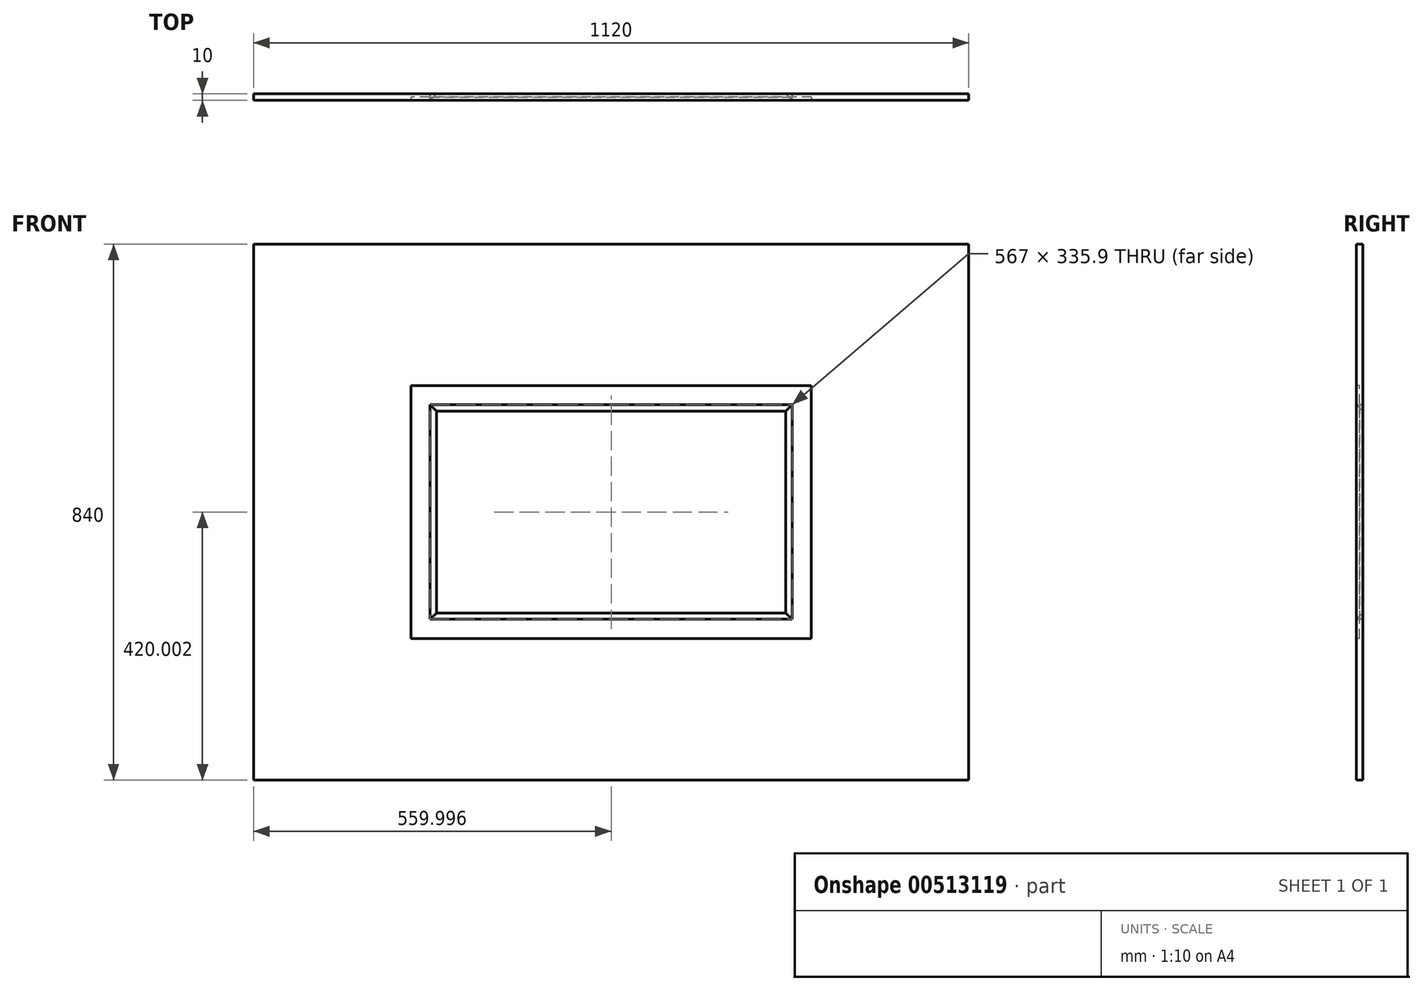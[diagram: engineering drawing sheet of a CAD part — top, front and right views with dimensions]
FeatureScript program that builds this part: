
annotation { "Feature Type Name" : "Feature", "Feature Type Description" : "" }
export const myFeature = defineFeature(function(context is Context, id is Id, definition is map)
    precondition{}
    {
        {
            var Q0;
            Q0=qCreatedBy(makeId("Front.planeOp"),FACE);
            var sketch = newSketch(context, id + "F0", { "sketchPlane" : qUnion([Q0])});
            skLineSegment(sketch, "E0.bottom", {"start": v(-285.87, 176.4) * mm, "end": v(281.13, 176.4) * mm});
            skLineSegment(sketch, "E0.top", {"start": v(-285.87, -159.5) * mm, "end": v(281.13, -159.5) * mm});
            skLineSegment(sketch, "E0.left", {"start": v(-285.87, 176.4) * mm, "end": v(-285.87, -159.5) * mm});
            skLineSegment(sketch, "E0.right", {"start": v(281.13, 176.4) * mm, "end": v(281.13, -159.5) * mm});
            skLineSegment(sketch, "E1", {"start": v(281.13, 176.4) * mm, "end": v(271.13, 166.4) * mm});
            skLineSegment(sketch, "E2", {"start": v(-285.87, -159.5) * mm, "end": v(-275.87, -149.5) * mm});
            skLineSegment(sketch, "E3.bottom", {"start": v(-275.87, -149.5) * mm, "end": v(271.13, -149.5) * mm});
            skLineSegment(sketch, "E3.top", {"start": v(-275.87, 166.4) * mm, "end": v(271.13, 166.4) * mm});
            skLineSegment(sketch, "E3.left", {"start": v(-275.87, -149.5) * mm, "end": v(-275.87, 166.4) * mm});
            skLineSegment(sketch, "E3.right", {"start": v(271.13, -149.5) * mm, "end": v(271.13, 166.4) * mm});
            skLineSegment(sketch, "E4", {"start": v(187.78, 166.4) * mm, "end": v(187.78, 176.4) * mm});
            skSolve(sketch);
        }
        {
            var Q0;
            {var subQ0=sQuery(id+"F0.wireOp",EDGE,"E0.left");Q0=makeQuery(id+"F0.imprint","IMPRINT",FACE,{"disambiguationData":[TD([[makeQuery(id+"F0.imprint","IMPRINT",EDGE,{"derivedFrom":subQ0}),1.0]])]});}
            var Q1;
            {var subQ0=sQuery(id+"F0.wireOp",EDGE,"E0.bottom");Q1=makeQuery(id+"F0.imprint","IMPRINT",FACE,{"disambiguationData":[TD([[makeQuery(id+"F0.imprint","IMPRINT",EDGE,{"derivedFrom":subQ0}),-1.0]])]});}
            var Q2;
            {var subQ0=sQuery(id+"F0.wireOp",EDGE,"E0.right");Q2=makeQuery(id+"F0.imprint","IMPRINT",FACE,{"disambiguationData":[TD([[makeQuery(id+"F0.imprint","IMPRINT",EDGE,{"derivedFrom":subQ0}),-1.0]])]});}
            var Q3;
            {var subQ0=sQuery(id+"F0.wireOp",EDGE,"E0.top");Q3=makeQuery(id+"F0.imprint","IMPRINT",FACE,{"disambiguationData":[TD([[makeQuery(id+"F0.imprint","IMPRINT",EDGE,{"derivedFrom":subQ0}),1.0]])]});}
            extrude(context, id + "F1", {"entities" : qUnion([Q0, Q1, Q2, Q3]), "depth" : 10 * mm, "offsetDistance" : 25 * mm});
        }
        {
            var Q0;
            Q0=makeQuery(id+"F1.opExtrude","CAP_FACE",FACE,{"disambiguationData":[OSD([sQuery(id+"F0.wireOp",EDGE,"E0.bottom"),sQuery(id+"F0.wireOp",EDGE,"E0.top"),sQuery(id+"F0.wireOp",EDGE,"E0.left"),sQuery(id+"F0.wireOp",EDGE,"E0.right"),sQuery(id+"F0.wireOp",EDGE,"E3.bottom"),sQuery(id+"F0.wireOp",EDGE,"E3.top"),sQuery(id+"F0.wireOp",EDGE,"E3.left"),sQuery(id+"F0.wireOp",EDGE,"E3.right")])],"isStart":false});
            var sketch = newSketch(context, id + "F2", { "sketchPlane" : qUnion([Q0])});
            skLineSegment(sketch, "E5", {"start": v(-2.37, 176.4) * mm, "end": v(-2.37, 418.44) * mm});
            skLineSegment(sketch, "E6", {"start": v(-552.37, 418.44) * mm, "end": v(-2.37, 418.44) * mm});
            skLineSegment(sketch, "E7", {"start": v(-2.37, 418.44) * mm, "end": v(547.63, 418.44) * mm});
            skLineSegment(sketch, "E8", {"start": v(-552.37, 418.44) * mm, "end": v(-552.37, -401.56) * mm});
            skLineSegment(sketch, "E9", {"start": v(-552.37, -401.56) * mm, "end": v(547.63, -401.56) * mm});
            skLineSegment(sketch, "E10", {"start": v(547.63, -401.56) * mm, "end": v(547.63, 418.44) * mm});
            skLineSegment(sketch, "E11", {"start": v(-285.87, 8.44) * mm, "end": v(-552.37, 8.44) * mm});
            skLineSegment(sketch, "E12.0", {"start": v(-2.37, 428.44) * mm, "end": v(557.63, 428.44) * mm});
            skLineSegment(sketch, "E12.1", {"start": v(557.63, -411.56) * mm, "end": v(557.63, 428.44) * mm});
            skLineSegment(sketch, "E12.2", {"start": v(-562.37, 428.44) * mm, "end": v(-2.37, 428.44) * mm});
            skLineSegment(sketch, "E12.3", {"start": v(-562.37, 428.44) * mm, "end": v(-562.37, -411.56) * mm});
            skLineSegment(sketch, "E12.4", {"start": v(-562.37, -411.56) * mm, "end": v(557.63, -411.56) * mm});
            skSolve(sketch);
        }
        {
            var Q0;
            {var subQ6=sQuery(id+"F2.wireOp",EDGE,"E5");Q0=makeQuery(id+"F2.imprint","IMPRINT",FACE,{"disambiguationData":[TD([[makeQuery(id+"F2.imprint","IMPRINT",EDGE,{"derivedFrom":subQ6}),1.0]])]});}
            var Q1;
            {var subQ5=sQuery(id+"F2.wireOp",EDGE,"E5");Q1=makeQuery(id+"F2.imprint","IMPRINT",FACE,{"disambiguationData":[TD([[makeQuery(id+"F2.imprint","IMPRINT",EDGE,{"derivedFrom":subQ5}),-1.0]])]});}
            var Q2;
            {var subQ1=sQuery(id+"F2.wireOp",EDGE,"E6");Q2=makeQuery(id+"F2.imprint","IMPRINT",FACE,{"disambiguationData":[TD([[makeQuery(id+"F2.imprint","IMPRINT",EDGE,{"derivedFrom":subQ1}),1.0]])]});}
            extrude(context, id + "F3", {"entities" : qUnion([Q0, Q1, Q2]), "oppositeDirection" : true, "depth" : 10 * mm, "offsetDistance" : 25 * mm});
        }
        {
            var Q0;
            Q0=makeQuery(id+"F1.opExtrude","CAP_EDGE",EDGE,{"disambiguationData":[OSD([sQuery(id+"F0.wireOp",EDGE,"E3.top")])],"isStart":false});
            var Q1;
            Q1=makeQuery(id+"F1.opExtrude","CAP_EDGE",EDGE,{"disambiguationData":[OSD([sQuery(id+"F0.wireOp",EDGE,"E3.right")])],"isStart":false});
            var Q2;
            Q2=makeQuery(id+"F1.opExtrude","CAP_EDGE",EDGE,{"disambiguationData":[OSD([sQuery(id+"F0.wireOp",EDGE,"E3.bottom")])],"isStart":false});
            var Q3;
            Q3=makeQuery(id+"F1.opExtrude","CAP_EDGE",EDGE,{"disambiguationData":[OSD([sQuery(id+"F0.wireOp",EDGE,"E3.left")])],"isStart":false});
            chamfer(context, id + "F4", {"entities" : qUnion([Q0, Q1, Q2, Q3]), "width" : 10 * mm, "tangentPropagation" : true});
        }
        {
            var Q0;
            Q0=makeQuery(id+"F3.opExtrude","CAP_FACE",FACE,{"disambiguationData":[OSD([sQuery(id+"F0.wireOp",EDGE,"E0.bottom"),sQuery(id+"F0.wireOp",EDGE,"E0.top"),sQuery(id+"F0.wireOp",EDGE,"E0.left"),sQuery(id+"F0.wireOp",EDGE,"E0.right"),sQuery(id+"F2.wireOp",EDGE,"E6"),sQuery(id+"F2.wireOp",EDGE,"E7"),sQuery(id+"F2.wireOp",EDGE,"E8"),sQuery(id+"F2.wireOp",EDGE,"E9"),sQuery(id+"F2.wireOp",EDGE,"E10")])],"isStart":true});
            var sketch = newSketch(context, id + "F5", { "sketchPlane" : qUnion([Q0])});
            skLineSegment(sketch, "E13", {"start": v(-285.87, 176.4) * mm, "end": v(-285.87, 206.4) * mm});
            skLineSegment(sketch, "E14", {"start": v(-285.87, 176.4) * mm, "end": v(-315.87, 176.4) * mm});
            skLineSegment(sketch, "E15", {"start": v(-315.87, 176.4) * mm, "end": v(-315.87, -216.51) * mm});
            skLineSegment(sketch, "E16", {"start": v(-285.87, 206.4) * mm, "end": v(410.55, 206.4) * mm});
            skLineSegment(sketch, "E17", {"start": v(281.13, -159.5) * mm, "end": v(281.13, -189.5) * mm});
            skLineSegment(sketch, "E18", {"start": v(281.13, -159.5) * mm, "end": v(311.13, -159.5) * mm});
            skLineSegment(sketch, "E19", {"start": v(281.13, -189.5) * mm, "end": v(-412.76, -189.5) * mm});
            skLineSegment(sketch, "E20", {"start": v(311.13, -159.5) * mm, "end": v(311.13, 293.34) * mm});
            skLineSegment(sketch, "E21", {"start": v(-315.87, 176.4) * mm, "end": v(-315.87, 281.44) * mm});
            skLineSegment(sketch, "E22", {"start": v(-285.87, 206.4) * mm, "end": v(-381.02, 206.4) * mm});
            skLineSegment(sketch, "E23", {"start": v(281.13, -189.5) * mm, "end": v(396.66, -189.5) * mm});
            skLineSegment(sketch, "E24", {"start": v(311.13, -159.5) * mm, "end": v(311.13, -264.13) * mm});
            skSolve(sketch);
        }
        {
            var Q0;
            {var subQ0=sQuery(id+"F5.wireOp",EDGE,"E13");Q0=makeQuery(id+"F5.imprint","IMPRINT",FACE,{"disambiguationData":[TD([[makeQuery(id+"F5.imprint","IMPRINT",EDGE,{"derivedFrom":subQ0}),1.0]])]});}
            var Q1;
            {var subQ2=sQuery(id+"F5.wireOp",EDGE,"E14");Q1=makeQuery(id+"F5.imprint","IMPRINT",FACE,{"disambiguationData":[TD([[makeQuery(id+"F5.imprint","IMPRINT",EDGE,{"derivedFrom":subQ2}),1.0]])]});}
            var Q2;
            {var subQ4=sQuery(id+"F5.wireOp",EDGE,"E13");Q2=makeQuery(id+"F5.imprint","IMPRINT",FACE,{"disambiguationData":[TD([[makeQuery(id+"F5.imprint","IMPRINT",EDGE,{"derivedFrom":subQ4}),-1.0]])]});}
            var Q3;
            {var subQ0=sQuery(id+"F5.wireOp",EDGE,"E17");Q3=makeQuery(id+"F5.imprint","IMPRINT",FACE,{"disambiguationData":[TD([[makeQuery(id+"F5.imprint","IMPRINT",EDGE,{"derivedFrom":subQ0}),1.0]])]});}
            extrude(context, id + "F6", {"entities" : qUnion([Q0, Q1, Q2, Q3]), "operationType" : NewBodyOperationType.REMOVE, "oppositeDirection" : true, "depth" : 5 * mm, "offsetDistance" : 25 * mm});
        }
    });
